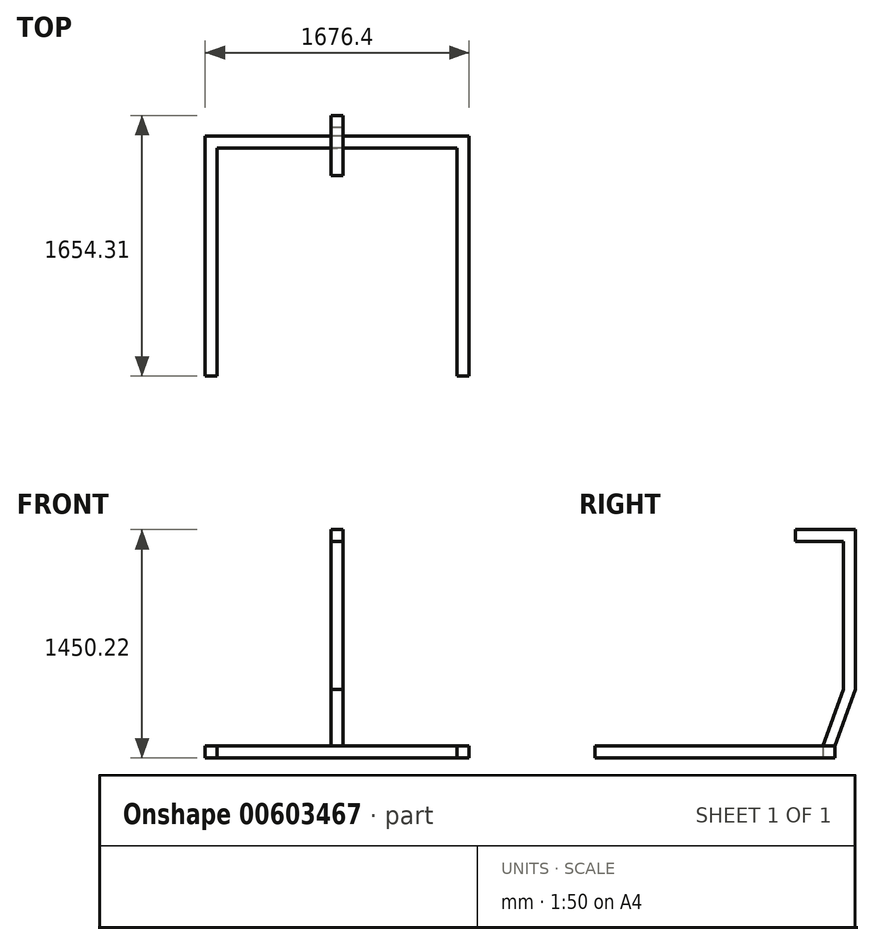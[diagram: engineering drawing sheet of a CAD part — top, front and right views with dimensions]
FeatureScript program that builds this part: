
annotation { "Feature Type Name" : "Feature", "Feature Type Description" : "" }
export const myFeature = defineFeature(function(context is Context, id is Id, definition is map)
    precondition{}
    {
        {
            var Q0;
            Q0=qCreatedBy(makeId("Top.planeOp"),FACE);
            var sketch = newSketch(context, id + "F0", { "sketchPlane" : qUnion([Q0])});
            skLineSegment(sketch, "E0", {"start": v(-838.2, -1066.8) * mm, "end": v(-762, -1066.8) * mm});
            skLineSegment(sketch, "E1", {"start": v(-762, -1066.8) * mm, "end": v(-762, 381) * mm});
            skLineSegment(sketch, "E2", {"start": v(-762, 381) * mm, "end": v(762, 381) * mm});
            skLineSegment(sketch, "E3", {"start": v(762, 381) * mm, "end": v(762, -1066.8) * mm});
            skLineSegment(sketch, "E4", {"start": v(762, -1066.8) * mm, "end": v(838.2, -1066.8) * mm});
            skLineSegment(sketch, "E5", {"start": v(838.2, -1066.8) * mm, "end": v(838.2, 457.2) * mm});
            skLineSegment(sketch, "E6", {"start": v(838.2, 457.2) * mm, "end": v(-838.2, 457.2) * mm});
            skLineSegment(sketch, "E7", {"start": v(-838.2, 457.2) * mm, "end": v(-838.2, -1066.8) * mm});
            skSolve(sketch);
        }
        {
            var Q0;
            Q0=makeQuery(id+"F0.imprint","IMPRINT",FACE,{"disambiguationData":[TD([[makeQuery(id+"F0.imprint","IMPRINT",EDGE,{"derivedFrom":sQuery(id+"F0.wireOp",EDGE,"E0")}),1.0]])]});
            extrude(context, id + "F1", {"entities" : qUnion([Q0]), "depth" : 76.2 * mm, "offsetDistance" : 25.4 * mm});
        }
        {
            var Q0;
            Q0=qCreatedBy(makeId("Right.planeOp"),FACE);
            var sketch = newSketch(context, id + "F2", { "sketchPlane" : qUnion([Q0])});
            skLineSegment(sketch, "E8", {"start": v(457.2, 0) * mm, "end": v(457.2, 76.2) * mm});
            skLineSegment(sketch, "E9", {"start": v(457.2, 76.2) * mm, "end": v(587.5, 434.22) * mm});
            skLineSegment(sketch, "E10", {"start": v(587.5, 434.22) * mm, "end": v(587.5, 1450.22) * mm});
            skLineSegment(sketch, "E11", {"start": v(587.5, 1450.22) * mm, "end": v(206.5, 1450.22) * mm});
            skLineSegment(sketch, "E12", {"start": v(206.5, 1450.22) * mm, "end": v(206.5, 1374.02) * mm});
            skLineSegment(sketch, "E13", {"start": v(206.5, 1374.02) * mm, "end": v(511.3, 1374.02) * mm});
            skLineSegment(sketch, "E14", {"start": v(511.3, 1374.02) * mm, "end": v(511.3, 434.22) * mm});
            skLineSegment(sketch, "E15", {"start": v(511.3, 434.22) * mm, "end": v(381, 76.2) * mm});
            skLineSegment(sketch, "E16", {"start": v(381, 76.2) * mm, "end": v(381, 0) * mm});
            skLineSegment(sketch, "E17", {"start": v(381, 0) * mm, "end": v(457.2, 0) * mm});
            skSolve(sketch);
        }
        {
            var Q0;
            Q0=makeQuery(id+"F2.imprint","IMPRINT",FACE,{"disambiguationData":[TD([[makeQuery(id+"F2.imprint","IMPRINT",EDGE,{"derivedFrom":sQuery(id+"F2.wireOp",EDGE,"E8")}),1.0]])]});
            extrude(context, id + "F3", {"entities" : qUnion([Q0]), "operationType" : NewBodyOperationType.ADD, "endBound" : BoundingType.SYMMETRIC, "depth" : 76.2 * mm, "offsetDistance" : 25.4 * mm});
        }
    });
